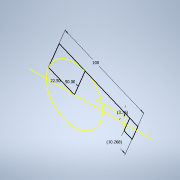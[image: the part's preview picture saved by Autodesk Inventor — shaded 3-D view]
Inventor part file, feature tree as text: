
AUTODESK INVENTOR PART (.ipt)
format: ipt  version: 2022 (Build 260153070, 153G)  size: 97,280 bytes
history: native  units: mm
features: other x5, reference x3, sketch x1
ambient origin geometry x8: Origin, YZ Plane, XZ Plane, XY Plane, X Axis, Y Axis, Z Axis, Center Point
feature tree (9):
  sketch  "Sketch1"  dims[d0=90.0deg d4=100.0mm d5=22.5deg d6=10.267698mm d7=3.760459mm]
  reference  "Reference1"
  reference  "Reference2"
  reference  "Reference3"
  other  "<userpath> laptop\Desktop\SumoBot\FullBot.iam"
  other  "FullBot.iam"
  other  "TT wheel:1"
  other  "MotorEncoderAssembly:1"
  other  "TTmotor:1"
